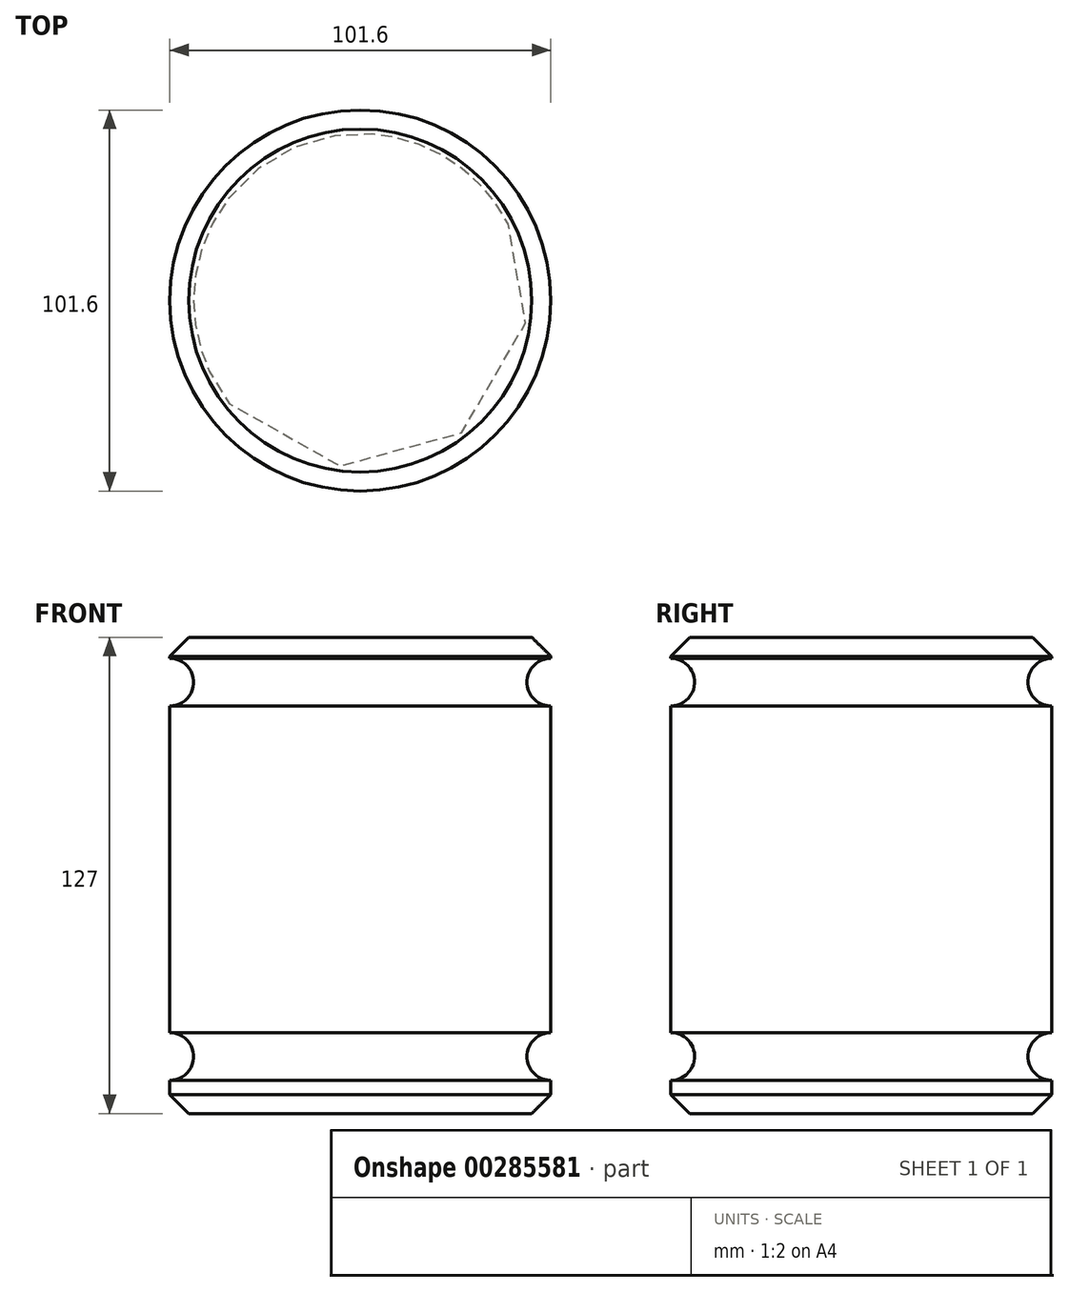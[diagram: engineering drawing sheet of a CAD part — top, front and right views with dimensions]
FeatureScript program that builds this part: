
annotation { "Feature Type Name" : "Feature", "Feature Type Description" : "" }
export const myFeature = defineFeature(function(context is Context, id is Id, definition is map)
    precondition{}
    {
        {
            var Q0;
            Q0=qCreatedBy(makeId("Front.planeOp"),FACE);
            var sketch = newSketch(context, id + "F0", { "sketchPlane" : qUnion([Q0])});
            skLineSegment(sketch, "E0.bottom", {"start": v(0, 0) * mm, "end": v(-50.8, 0) * mm});
            skLineSegment(sketch, "E0.top", {"start": v(0, 127) * mm, "end": v(-50.8, 127) * mm});
            skLineSegment(sketch, "E0.left", {"start": v(0, 0) * mm, "end": v(0, 8.87) * mm});
            skLineSegment(sketch, "E0.right", {"start": v(-50.8, 0) * mm, "end": v(-50.8, 127) * mm});
            skArc(sketch, "E1", {"start": v(0, 121.37) * mm, "mid": v(-6.35, 115.02) * mm, "end": v(0, 108.67) * mm});
            skArc(sketch, "E2", {"start": v(0, 21.57) * mm, "mid": v(-6.35, 15.22) * mm, "end": v(0, 8.87) * mm});
            skLineSegment(sketch, "E3.trimOffspring", {"start": v(0, 121.37) * mm, "end": v(0, 127) * mm});
            skLineSegment(sketch, "E4.trimOffspring", {"start": v(0, 21.57) * mm, "end": v(0, 108.67) * mm});
            skSolve(sketch);
        }
        {
            var Q0;
            Q0=makeQuery(id+"F0.imprint","IMPRINT",FACE,{"disambiguationData":[TD([[makeQuery(id+"F0.imprint","IMPRINT",EDGE,{"derivedFrom":sQuery(id+"F0.wireOp",EDGE,"E0.bottom")}),-1.0]])]});
            var Q1;
            Q1=sQuery(id+"F0.wireOp",EDGE,"E0.right");
            revolve(context, id + "F1", {"entities" : qUnion([Q0]), "axis" : qUnion([Q1]), "revolveType" : RevolveType.FULL});
        }
        {
            var Q0;
            Q0=makeQuery(id+"F1.opRevolve","SWEPT_FACE",FACE,{"disambiguationData":[OSD([sQuery(id+"F0.wireOp",EDGE,"E0.top")])]});
            var Q1;
            Q1=makeQuery(id+"F1.opRevolve","SWEPT_FACE",FACE,{"disambiguationData":[OSD([sQuery(id+"F0.wireOp",EDGE,"E0.bottom")])]});
            chamfer(context, id + "F2", {"entities" : qUnion([Q0, Q1]), "width" : 5.08 * mm, "tangentPropagation" : true});
        }
    });
